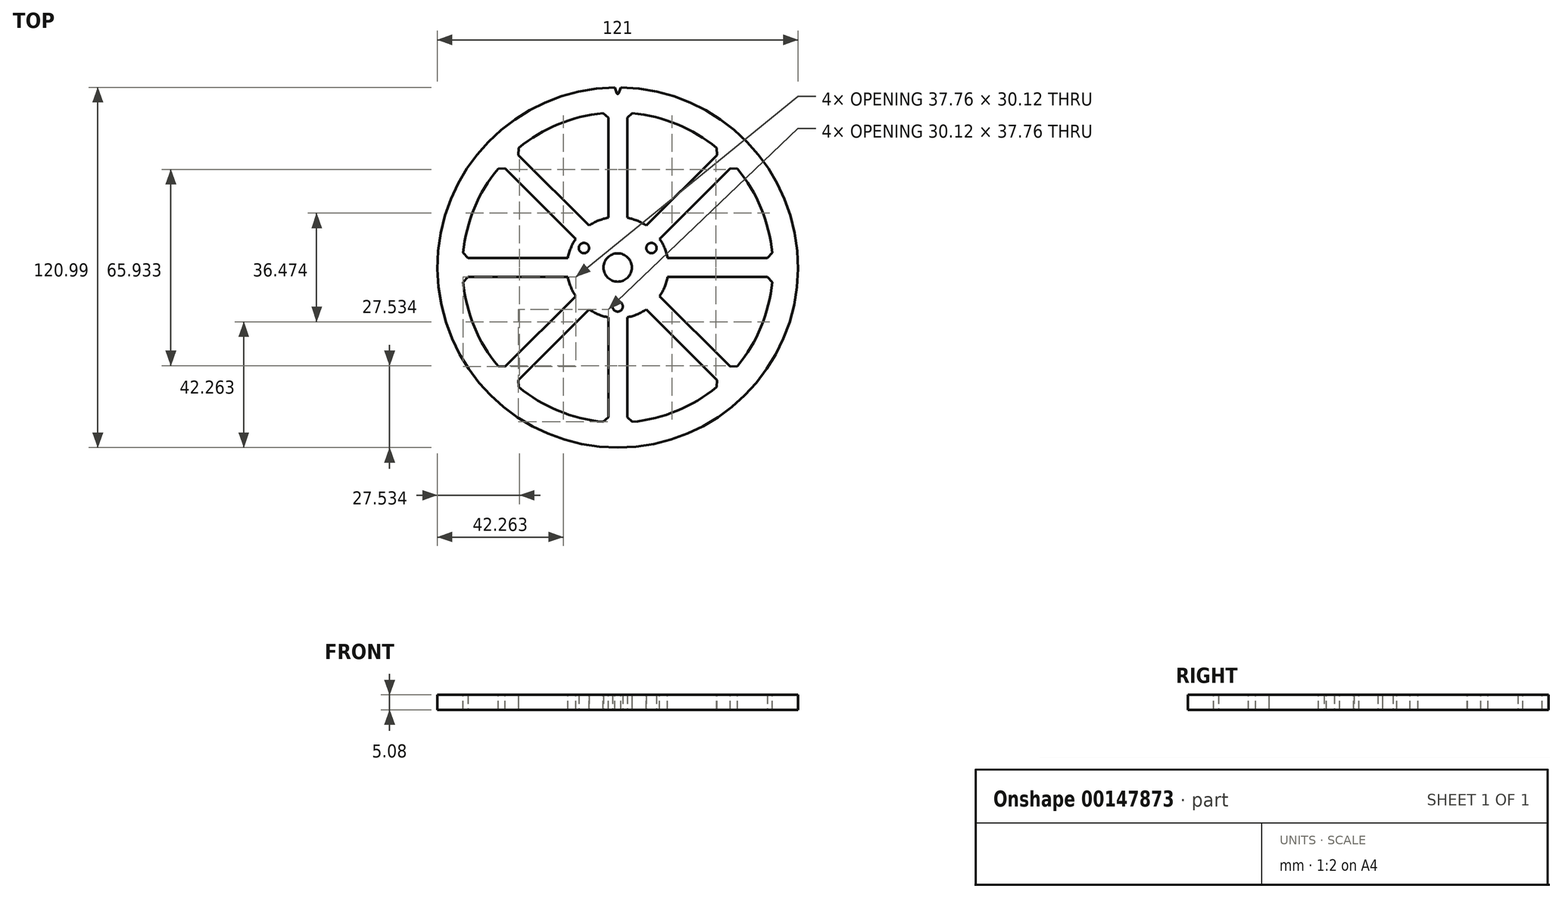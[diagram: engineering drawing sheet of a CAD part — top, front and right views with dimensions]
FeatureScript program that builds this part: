
annotation { "Feature Type Name" : "Feature", "Feature Type Description" : "" }
export const myFeature = defineFeature(function(context is Context, id is Id, definition is map)
    precondition{}
    {
        {
            var Q0;
            Q0=qCreatedBy(makeId("Top.planeOp"),FACE);
            var sketch = newSketch(context, id + "F0", { "sketchPlane" : qUnion([Q0])});
            skCircle(sketch, "E0", {"center": v(0, 0) * mm, "radius": 60.5 * mm});
            skCircle(sketch, "E1", {"center": v(0, 0) * mm, "radius": 4.76 * mm});
            skCircle(sketch, "E2", {"center": v(0, 0) * mm, "radius": 17.04 * mm, "construction": true});
            skCircle(sketch, "E3.cCircle", {"center": v(0, 0) * mm, "radius": 6.54 * mm, "construction": true});
            skLineSegment(sketch, "E3.0", {"start": v(-11.32, 6.54) * mm, "end": v(11.32, 6.54) * mm, "construction": true});
            skLineSegment(sketch, "E3.1", {"start": v(11.32, 6.54) * mm, "end": v(0, -13.07) * mm, "construction": true});
            skLineSegment(sketch, "E3.2", {"start": v(0, -13.07) * mm, "end": v(-11.32, 6.54) * mm, "construction": true});
            skPoint(sketch, "E3.0.midPoint", {"position": v(0, 6.54) * mm});
            skCircle(sketch, "E4", {"center": v(-11.32, 6.54) * mm, "radius": 3.97 * mm, "construction": true});
            skCircle(sketch, "E5", {"center": v(-11.32, 6.54) * mm, "radius": 1.73 * mm});
            skCircle(sketch, "E6", {"center": v(11.32, 6.54) * mm, "radius": 1.73 * mm});
            skCircle(sketch, "E7", {"center": v(0, -13.07) * mm, "radius": 1.73 * mm});
            skSolve(sketch);
        }
        {
            var Q0;
            Q0=makeQuery(id+"F0.imprint","IMPRINT",FACE,{"disambiguationData":[TD([[makeQuery(id+"F0.imprint","IMPRINT",EDGE,{"derivedFrom":sQuery(id+"F0.wireOp",EDGE,"d7zeTPih-CRss-xDOh-gPdP-rmPCdwzH7cdN.left")}),1.0]])]});
            var Q1;
            Q1=makeQuery(id+"F0.imprint","IMPRINT",FACE,{"disambiguationData":[TD([[makeQuery(id+"F0.imprint","IMPRINT",EDGE,{"derivedFrom":sQuery(id+"F0.wireOp",EDGE,"E0")}),1.0]])]});
            extrude(context, id + "F1", {"entities" : qUnion([Q0, Q1]), "depth" : 5.08 * mm});
        }
        {
            var Q0;
            Q0=makeQuery(id+"F1.opExtrude","CAP_FACE",FACE,{"disambiguationData":[OSD([sQuery(id+"F0.wireOp",EDGE,"d7zeTPih-CRss-xDOh-gPdP-rmPCdwzH7cdN.left"),sQuery(id+"F0.wireOp",EDGE,"d7zeTPih-CRss-xDOh-gPdP-rmPCdwzH7cdN.right"),sQuery(id+"F0.wireOp",EDGE,"ScfBMfkV-s1yN-Ls9R-SGr5-fEyGpD6zak8e"),sQuery(id+"F0.wireOp",EDGE,"xnxmVwjl-FvSF-m7sj-be2U-u85gZZGoORGZ"),sQuery(id+"F0.wireOp",EDGE,"E0")])],"isStart":false});
            var sketch = newSketch(context, id + "F2", { "sketchPlane" : qUnion([Q0])});
            skLineSegment(sketch, "E8", {"start": v(0, 0) * mm, "end": v(0, 60.5) * mm, "construction": true});
            skLineSegment(sketch, "E9", {"start": v(0, 0) * mm, "end": v(0.66, 60.5) * mm, "construction": true});
            skArc(sketch, "E10", {"start": v(1.02, 60.5) * mm, "mid": v(0, 60.5) * mm, "end": v(-1.02, 60.5) * mm});
            skLineSegment(sketch, "E11", {"start": v(-1.02, 60.5) * mm, "end": v(-0.28, 58.52) * mm});
            skLineSegment(sketch, "E12", {"start": v(1.02, 60.5) * mm, "end": v(0.28, 58.52) * mm});
            skPoint(sketch, "E13", {"position": v(0.65, 59.5) * mm});
            skArc(sketch, "E14", {"start": v(-0.28, 58.52) * mm, "mid": v(0, 58.33) * mm, "end": v(0.28, 58.52) * mm});
            skSolve(sketch);
        }
        {
            var Q0;
            Q0=qSketchRegion(id+"F2",true);
            var Q1;
            Q1=makeQuery(id+"F1.opExtrude","CAP_FACE",FACE,{"disambiguationData":[OSD([sQuery(id+"F0.wireOp",EDGE,"d7zeTPih-CRss-xDOh-gPdP-rmPCdwzH7cdN.left"),sQuery(id+"F0.wireOp",EDGE,"d7zeTPih-CRss-xDOh-gPdP-rmPCdwzH7cdN.right"),sQuery(id+"F0.wireOp",EDGE,"ScfBMfkV-s1yN-Ls9R-SGr5-fEyGpD6zak8e"),sQuery(id+"F0.wireOp",EDGE,"xnxmVwjl-FvSF-m7sj-be2U-u85gZZGoORGZ"),sQuery(id+"F0.wireOp",EDGE,"E0")])],"isStart":true});
            extrude(context, id + "F3", {"entities" : qUnion([Q0]), "operationType" : NewBodyOperationType.REMOVE, "endBound" : BoundingType.UP_TO_SURFACE, "oppositeDirection" : true, "endBoundEntityFace" : qUnion([Q1]), "depth" : 25.4 * mm});
        }
        {
            var Q0;
            Q0=makeQuery(id+"F1.opExtrude","CAP_FACE",FACE,{"disambiguationData":[OSD([sQuery(id+"F0.wireOp",EDGE,"E0"),sQuery(id+"F0.wireOp",EDGE,"E1"),sQuery(id+"F0.wireOp",EDGE,"tRzARMfv-7BFj-HnuO-QooS-YK2TcsRHxJGM"),sQuery(id+"F0.wireOp",EDGE,"l2f0ixeT-HVOn-P7pL-0EBq-9Ms4uDoOWkmK"),sQuery(id+"F0.wireOp",EDGE,"czIBXI4K-ms6v-gZLf-gVDV-WxWQWUw0xqfL"),sQuery(id+"F0.wireOp",EDGE,"zD3yCDk3-du4V-XvNA-neFI-n9ijwsGpr5Hr")])],"isStart":false});
            var sketch = newSketch(context, id + "F4", { "sketchPlane" : qUnion([Q0])});
            skLineSegment(sketch, "E15", {"start": v(0, 0) * mm, "end": v(0, 16.75) * mm, "construction": true});
            skLineSegment(sketch, "E16", {"start": v(0, 16.75) * mm, "end": v(3.18, 16.75) * mm, "construction": true});
            skLineSegment(sketch, "E17", {"start": v(3.18, 16.75) * mm, "end": v(3.18, 51.98) * mm});
            skLineSegment(sketch, "E18", {"start": v(3.18, 51.98) * mm, "end": v(0, 51.98) * mm, "construction": true});
            skLineSegment(sketch, "E19", {"start": v(0, 51.98) * mm, "end": v(0, 58.33) * mm, "construction": true});
            skCircle(sketch, "E20", {"center": v(0, 0) * mm, "radius": 58.33 * mm, "construction": true});
            skArc(sketch, "E21", {"start": v(9.6, 14.09) * mm, "mid": v(6.52, 15.75) * mm, "end": v(3.18, 16.75) * mm});
            skLineSegment(sketch, "E22", {"start": v(0, 0) * mm, "end": v(11.84, 11.84) * mm, "construction": true});
            skLineSegment(sketch, "E23", {"start": v(11.84, 11.84) * mm, "end": v(9.6, 14.09) * mm, "construction": true});
            skLineSegment(sketch, "E24", {"start": v(9.6, 14.09) * mm, "end": v(34.51, 39) * mm});
            skArc(sketch, "E25", {"start": v(34.51, 39) * mm, "mid": v(19.93, 48.11) * mm, "end": v(3.17, 51.98) * mm});
            skSolve(sketch);
        }
        {
            var Q0;
            Q0=qSketchRegion(id+"F4",true);
            var Q1;
            Q1=makeQuery(id+"F1.opExtrude","SWEPT_BODY",BODY,{"disambiguationData":[OSD([sQuery(id+"F0.wireOp",EDGE,"E0"),sQuery(id+"F0.wireOp",EDGE,"E1"),sQuery(id+"F0.wireOp",EDGE,"tRzARMfv-7BFj-HnuO-QooS-YK2TcsRHxJGM"),sQuery(id+"F0.wireOp",EDGE,"l2f0ixeT-HVOn-P7pL-0EBq-9Ms4uDoOWkmK"),sQuery(id+"F0.wireOp",EDGE,"czIBXI4K-ms6v-gZLf-gVDV-WxWQWUw0xqfL"),sQuery(id+"F0.wireOp",EDGE,"zD3yCDk3-du4V-XvNA-neFI-n9ijwsGpr5Hr")])]});
            extrude(context, id + "F5", {"entities" : qUnion([Q0]), "operationType" : NewBodyOperationType.REMOVE, "endBound" : BoundingType.UP_TO_BODY, "oppositeDirection" : true, "endBoundEntityBody" : qUnion([Q1]), "depth" : 25.4 * mm});
        }
        {
            var Q0;
            Q0=makeQuery(id+"F5.boolean.opBoolean","COPY",EDGE,{"derivedFrom":makeQuery(id+"F5.opExtrude","SWEPT_EDGE",EDGE,{"disambiguationData":[OSD([sQuery(id+"F4.wireOp",EDGE,"E17"),sQuery(id+"F4.wireOp",EDGE,"E25")])]})});
            var Q1;
            Q1=makeQuery(id+"F5.boolean.opBoolean","COPY",EDGE,{"derivedFrom":makeQuery(id+"F5.opExtrude","SWEPT_EDGE",EDGE,{"disambiguationData":[OSD([sQuery(id+"F4.wireOp",EDGE,"E24"),sQuery(id+"F4.wireOp",EDGE,"E25")])]})});
            chamfer(context, id + "F6", {"entities" : qUnion([Q0, Q1]), "width" : 1.59 * mm, "tangentPropagation" : true});
        }
        {
            var Q0;
            Q0=makeQuery(id+"F5.boolean.opBoolean","COPY",FACE,{"derivedFrom":makeQuery(id+"F5.opExtrude","SWEPT_FACE",FACE,{"disambiguationData":[OSD([sQuery(id+"F4.wireOp",EDGE,"E21")])]})});
            var Q1;
            Q1=makeQuery(id+"F5.boolean.opBoolean","COPY",FACE,{"derivedFrom":makeQuery(id+"F5.opExtrude","SWEPT_FACE",FACE,{"disambiguationData":[OSD([sQuery(id+"F4.wireOp",EDGE,"E17")])]})});
            var Q2;
            Q2=makeQuery(id+"F5.boolean.opBoolean","COPY",FACE,{"derivedFrom":makeQuery(id+"F5.opExtrude","SWEPT_FACE",FACE,{"disambiguationData":[OSD([sQuery(id+"F4.wireOp",EDGE,"E24")])]})});
            var Q3;
            Q3=makeQuery(id+"F6.opChamfer","BLEND_FACE",FACE,{"disambiguationData":[OSD([sQuery(id+"F4.wireOp",EDGE,"E24"),sQuery(id+"F4.wireOp",EDGE,"E25")])]});
            var Q4;
            Q4=makeQuery(id+"F5.boolean.opBoolean","COPY",FACE,{"derivedFrom":makeQuery(id+"F5.opExtrude","SWEPT_FACE",FACE,{"disambiguationData":[OSD([sQuery(id+"F4.wireOp",EDGE,"E25")])]})});
            var Q5;
            Q5=makeQuery(id+"F6.opChamfer","BLEND_FACE",FACE,{"disambiguationData":[OSD([sQuery(id+"F4.wireOp",EDGE,"E17"),sQuery(id+"F4.wireOp",EDGE,"E25")])]});
            var Q6;
            Q6=makeQuery(id+"F1.opExtrude","SWEPT_FACE",FACE,{"disambiguationData":[OSD([sQuery(id+"F0.wireOp",EDGE,"E1")])]});
            circularPattern(context, id + "F7", {"patternType" : PatternType.FACE, "faces" : qUnion([Q0, Q1, Q2, Q3, Q4, Q5]), "axis" : qUnion([Q6]), "angle" : 45 * degree, "instanceCount" : 8});
        }
    });
